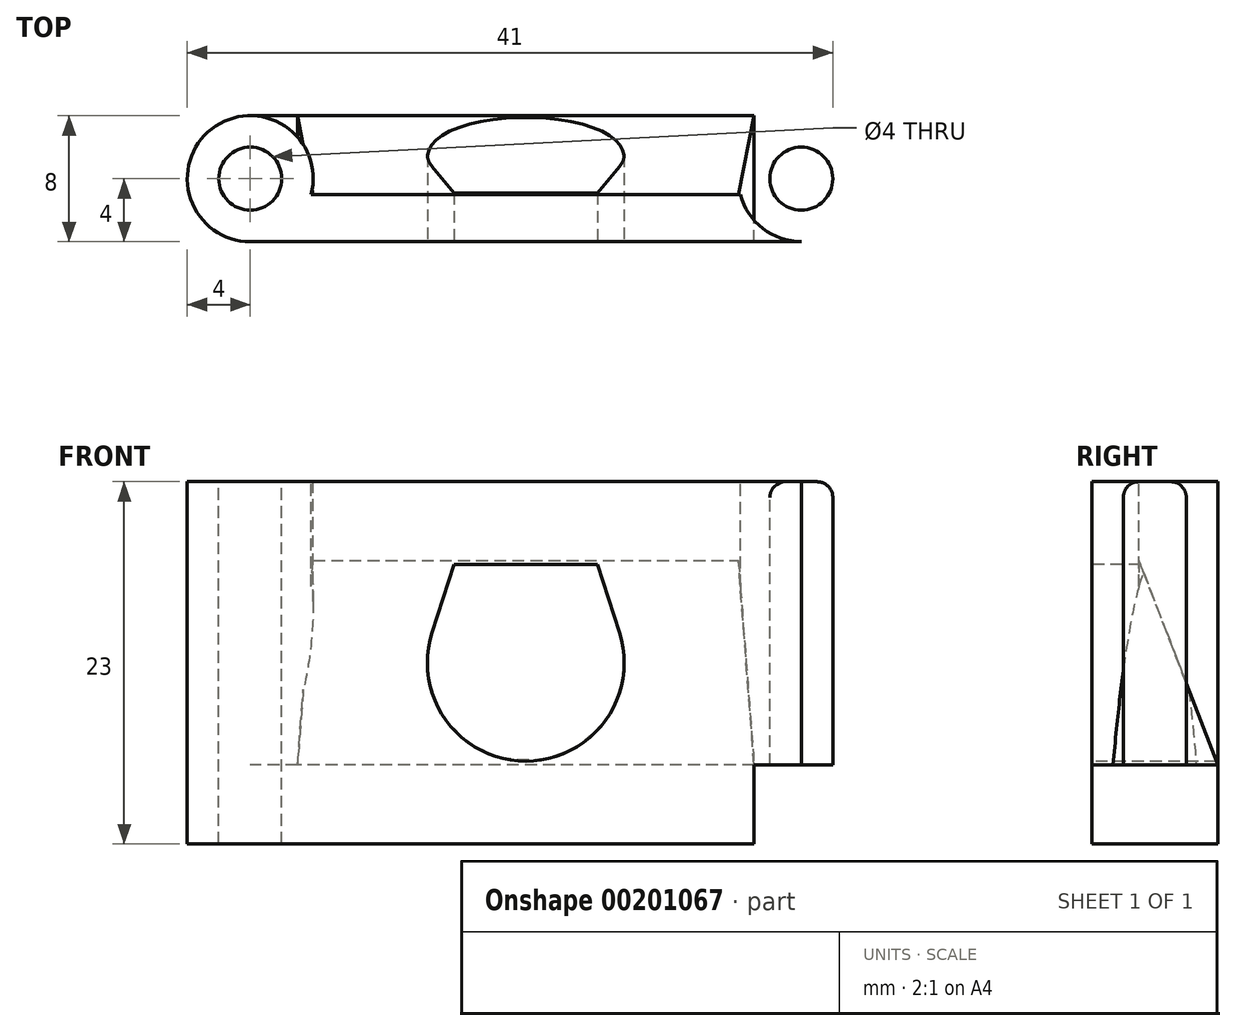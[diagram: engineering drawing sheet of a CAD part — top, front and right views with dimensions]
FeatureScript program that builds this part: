
annotation { "Feature Type Name" : "Feature", "Feature Type Description" : "" }
export const myFeature = defineFeature(function(context is Context, id is Id, definition is map)
    precondition{}
    {
        {
            var Q0;
            Q0=qCreatedBy(makeId("Top.planeOp"),FACE);
            var sketch = newSketch(context, id + "F0", { "sketchPlane" : qUnion([Q0])});
            skLineSegment(sketch, "E0.bottom", {"start": v(17.5, -4) * mm, "end": v(-17.5, -4) * mm});
            skLineSegment(sketch, "E0.top", {"start": v(17.5, 4) * mm, "end": v(-17.5, 4) * mm});
            skPoint(sketch, "E0.middle", {"position": v(0, 0) * mm});
            skArc(sketch, "E1", {"start": v(-17.5, 4) * mm, "mid": v(-21.5, 0) * mm, "end": v(-17.5, -4) * mm});
            skCircle(sketch, "E2", {"center": v(-17.5, 0) * mm, "radius": 2 * mm});
            skArc(sketch, "E3.MirrorCS", {"start": v(17.5, 4) * mm, "mid": v(21.5, 0) * mm, "end": v(17.5, -4) * mm});
            skCircle(sketch, "E4.MirrorC", {"center": v(17.5, 0) * mm, "radius": 2 * mm});
            skPoint(sketch, "E5.start.orphan", {"position": v(-15.5, 0) * mm});
            skPoint(sketch, "E6.start.orphan", {"position": v(15.5, 0) * mm});
            skPoint(sketch, "E7.start.orphan", {"position": v(-15.5, -4) * mm});
            skPoint(sketch, "E8.orphan", {"position": v(15.5, -4) * mm});
            skPoint(sketch, "E9.start.orphan", {"position": v(15.5, 4) * mm});
            skLineSegment(sketch, "E10", {"start": v(14.5, -4) * mm, "end": v(14.5, 4) * mm});
            skLineSegment(sketch, "E11", {"start": v(-14.5, 4) * mm, "end": v(-14.5, -4) * mm});
            skSolve(sketch);
        }
        {
            var Q0;
            Q0=qCreatedBy(makeId("Top.planeOp"),FACE);
            cPlane(context, id + "F1", {"entities" : qUnion([Q0]), "cplaneType" : CPlaneType.OFFSET, "offset" : 13 * mm, "width" : 150 * mm, "height" : 150 * mm});
        }
        {
            var Q0;
            Q0=qCreatedBy(id+"F1.planeOp",FACE);
            var sketch = newSketch(context, id + "F2", { "sketchPlane" : qUnion([Q0])});
            skLineSegment(sketch, "E12.bottom", {"start": v(-17.5, -4) * mm, "end": v(17.5, -4) * mm});
            skLineSegment(sketch, "E12.top", {"start": v(-13.63, -1) * mm, "end": v(13.63, -1) * mm});
            skCircle(sketch, "E13", {"center": v(-17.5, 0) * mm, "radius": 4 * mm});
            skCircle(sketch, "E14", {"center": v(-17.5, 0) * mm, "radius": 2 * mm});
            skCircle(sketch, "E15.MirrorC", {"center": v(17.5, 0) * mm, "radius": 4 * mm});
            skCircle(sketch, "E16.MirrorC", {"center": v(17.5, 0) * mm, "radius": 2 * mm});
            skLineSegment(sketch, "E17", {"start": v(-13.5, -1) * mm, "end": v(-13.5, -4) * mm});
            skLineSegment(sketch, "E18", {"start": v(13.5, -1) * mm, "end": v(13.5, -4) * mm});
            skPoint(sketch, "E19.orphan", {"position": v(-13.5, 0) * mm});
            skPoint(sketch, "E20.orphan", {"position": v(13.5, 0) * mm});
            skSolve(sketch);
        }
        {
            var Q0;
            {var subQ0=sQuery(id+"F0.wireOp",EDGE,"E10");Q0=makeQuery(id+"F0.imprint","IMPRINT",FACE,{"disambiguationData":[TD([[makeQuery(id+"F0.imprint","IMPRINT",EDGE,{"derivedFrom":subQ0}),1.0]])]});}
            var Q1;
            {var subQ0=sQuery(id+"F2.wireOp",EDGE,"E17");Q1=makeQuery(id+"F2.imprint","IMPRINT",FACE,{"disambiguationData":[TD([[makeQuery(id+"F2.imprint","IMPRINT",EDGE,{"derivedFrom":subQ0}),1.0]])]});}
            loft(context, id + "F3", {"sheetProfilesArray" : [{ "sheetProfileEntities" : qUnion([Q0]) }, { "sheetProfileEntities" : qUnion([Q1]) }]});
        }
        {
            var Q0;
            {var subQ3=sQuery(id+"F2.wireOp",EDGE,"E18");Q0=makeQuery(id+"F2.imprint","IMPRINT",FACE,{"disambiguationData":[TD([[makeQuery(id+"F2.imprint","IMPRINT",EDGE,{"derivedFrom":subQ3}),1.0]])]});}
            var Q1;
            Q1=makeQuery(id+"F2.imprint","IMPRINT",FACE,{"disambiguationData":[TD([[makeQuery(id+"F2.imprint","IMPRINT",EDGE,{"derivedFrom":sQuery(id+"F2.wireOp",EDGE,"E16.MirrorC")}),1.0]])]});
            var Q2;
            Q2=makeQuery(id+"F2.imprint","IMPRINT",FACE,{"disambiguationData":[TD([[makeQuery(id+"F2.imprint","IMPRINT",EDGE,{"derivedFrom":sQuery(id+"F2.wireOp",EDGE,"E14")}),-1.0]])]});
            var Q3;
            {var subQ3=sQuery(id+"F2.wireOp",EDGE,"E17");Q3=makeQuery(id+"F2.imprint","IMPRINT",FACE,{"disambiguationData":[TD([[makeQuery(id+"F2.imprint","IMPRINT",EDGE,{"derivedFrom":subQ3}),-1.0]])]});}
            extrude(context, id + "F4", {"entities" : qUnion([Q0, Q1, Q2, Q3]), "operationType" : NewBodyOperationType.ADD, "oppositeDirection" : true, "depth" : 13 * mm});
        }
        {
            var Q0;
            {var subQ0=sQuery(id+"F2.wireOp",EDGE,"E12.bottom");var subQ1=sQuery(id+"F2.wireOp",EDGE,"E18");var subQ2=sQuery(id+"F2.wireOp",EDGE,"E17");Q0=makeQuery(id+"F4.boolean.opBoolean","MERGE",FACE,{"derivedFrom":[makeQuery(id+"F3.opLoft","SWEPT_FACE",FACE,{"disambiguationData":[OSD([sQuery(id+"F0.wireOp",EDGE,"E0.bottom"),sQuery(id+"F0.wireOp",EDGE,"E10"),sQuery(id+"F0.wireOp",EDGE,"E11"),subQ0,subQ2,subQ1])]}),makeQuery(id+"F4.opExtrude","SWEPT_FACE",FACE,{"disambiguationData":[OSD([subQ0]),TDD([makeQuery(id+"F2.imprint","IMPRINT",EDGE,{"disambiguationData":[TD([[makeQuery(id+"F2.imprint","INTERSECT",VERTEX,{"derivedFrom":[subQ0,sQuery(id+"F2.wireOp",EDGE,"E13")]}),-1.0]])],"derivedFrom":subQ0})])]}),makeQuery(id+"F4.opExtrude","SWEPT_FACE",FACE,{"disambiguationData":[OSD([subQ0]),TDD([makeQuery(id+"F2.imprint","IMPRINT",EDGE,{"disambiguationData":[TD([[makeQuery(id+"F2.imprint","INTERSECT",VERTEX,{"derivedFrom":[subQ0,sQuery(id+"F2.wireOp",EDGE,"E15.MirrorC")]}),1.0]])],"derivedFrom":subQ0})])]})]});}
            var sketch = newSketch(context, id + "F5", { "sketchPlane" : qUnion([Q0])});
            skArc(sketch, "E21", {"start": v(-5.94, 8.43) * mm, "mid": v(0, 0.25) * mm, "end": v(5.94, 8.43) * mm});
            skLineSegment(sketch, "E22", {"start": v(0, 13) * mm, "end": v(0, 0) * mm, "construction": true});
            skArc(sketch, "E23.cCircle", {"start": v(-5.94, 8.43) * mm, "mid": v(0, 0.25) * mm, "end": v(5.94, 8.43) * mm, "construction": true});
            skLineSegment(sketch, "E23.0", {"start": v(-4.54, 12.75) * mm, "end": v(4.54, 12.75) * mm});
            skLineSegment(sketch, "E23.1", {"start": v(4.54, 12.75) * mm, "end": v(5.94, 8.43) * mm});
            skLineSegment(sketch, "E23.4", {"start": v(-5.94, 8.43) * mm, "end": v(-4.54, 12.75) * mm});
            skPoint(sketch, "E23.0.midPoint", {"position": v(0, 12.75) * mm});
            skPoint(sketch, "E24.orphan", {"position": v(7.35, 4.11) * mm});
            skPoint(sketch, "E25.orphan", {"position": v(-7.35, 4.11) * mm});
            skSolve(sketch);
        }
        {
            var Q0;
            Q0=makeQuery(id+"F5.imprint","IMPRINT",FACE,{"disambiguationData":[TD([[makeQuery(id+"F5.imprint","IMPRINT",EDGE,{"derivedFrom":sQuery(id+"F5.wireOp",EDGE,"E21")}),1.0]])]});
            extrude(context, id + "F6", {"entities" : qUnion([Q0]), "operationType" : NewBodyOperationType.REMOVE, "oppositeDirection" : true, "depth" : 25 * mm});
        }
        {
            var Q0;
            {var subQ0=sQuery(id+"F2.wireOp",EDGE,"E17");Q0=makeQuery(id+"F2.imprint","IMPRINT",FACE,{"disambiguationData":[TD([[makeQuery(id+"F2.imprint","IMPRINT",EDGE,{"derivedFrom":subQ0}),1.0]])]});}
            var Q1;
            {var subQ3=sQuery(id+"F2.wireOp",EDGE,"E17");Q1=makeQuery(id+"F2.imprint","IMPRINT",FACE,{"disambiguationData":[TD([[makeQuery(id+"F2.imprint","IMPRINT",EDGE,{"derivedFrom":subQ3}),-1.0]])]});}
            var Q2;
            Q2=makeQuery(id+"F2.imprint","IMPRINT",FACE,{"disambiguationData":[TD([[makeQuery(id+"F2.imprint","IMPRINT",EDGE,{"derivedFrom":sQuery(id+"F2.wireOp",EDGE,"E14")}),-1.0]])]});
            var Q3;
            Q3=makeQuery(id+"F2.imprint","IMPRINT",FACE,{"disambiguationData":[TD([[makeQuery(id+"F2.imprint","IMPRINT",EDGE,{"derivedFrom":sQuery(id+"F2.wireOp",EDGE,"E16.MirrorC")}),1.0]])]});
            var Q4;
            {var subQ3=sQuery(id+"F2.wireOp",EDGE,"E18");Q4=makeQuery(id+"F2.imprint","IMPRINT",FACE,{"disambiguationData":[TD([[makeQuery(id+"F2.imprint","IMPRINT",EDGE,{"derivedFrom":subQ3}),1.0]])]});}
            extrude(context, id + "F7", {"entities" : qUnion([Q0, Q1, Q2, Q3, Q4]), "operationType" : NewBodyOperationType.ADD, "depth" : 5 * mm});
        }
        {
            var Q0;
            {var subQ0=sQuery(id+"F0.wireOp",EDGE,"E10");Q0=makeQuery(id+"F0.imprint","IMPRINT",FACE,{"disambiguationData":[TD([[makeQuery(id+"F0.imprint","IMPRINT",EDGE,{"derivedFrom":subQ0}),1.0]])]});}
            var Q1;
            {var subQ0=sQuery(id+"F0.wireOp",EDGE,"E1");Q1=makeQuery(id+"F0.imprint","IMPRINT",FACE,{"disambiguationData":[TD([[makeQuery(id+"F0.imprint","IMPRINT",EDGE,{"derivedFrom":subQ0}),1.0]])]});}
            var Q2;
            {var subQ0=sQuery(id+"F0.wireOp",EDGE,"E3.MirrorCS");Q2=makeQuery(id+"F0.imprint","IMPRINT",FACE,{"disambiguationData":[TD([[makeQuery(id+"F0.imprint","IMPRINT",EDGE,{"derivedFrom":subQ0}),-1.0]])]});}
            extrude(context, id + "F8", {"entities" : qUnion([Q0, Q1, Q2]), "operationType" : NewBodyOperationType.ADD, "oppositeDirection" : true, "depth" : 5 * mm});
        }
        {
            var Q0;
            Q0=makeQuery(id+"F7.opExtrude","CAP_EDGE",EDGE,{"disambiguationData":[OSD([sQuery(id+"F2.wireOp",EDGE,"E12.top")])],"isStart":false});
            var Q1;
            Q1=makeQuery(id+"F7.opExtrude","CAP_EDGE",EDGE,{"disambiguationData":[OSD([sQuery(id+"F2.wireOp",EDGE,"E15.MirrorC")])],"isStart":false});
            var Q2;
            Q2=makeQuery(id+"F8.opExtrude","CAP_EDGE",EDGE,{"disambiguationData":[OSD([sQuery(id+"F0.wireOp",EDGE,"E0.top")])],"isStart":false});
            var Q3;
            Q3=makeQuery(id+"F7.opExtrude","CAP_EDGE",EDGE,{"disambiguationData":[OSD([sQuery(id+"F2.wireOp",EDGE,"E14")])],"isStart":false});
            var Q4;
            Q4=makeQuery(id+"F7.opExtrude","CAP_EDGE",EDGE,{"disambiguationData":[OSD([sQuery(id+"F2.wireOp",EDGE,"E16.MirrorC")])],"isStart":false});
            var Q5;
            Q5=makeQuery(id+"F6.boolean.opBoolean","COPY",EDGE,{"derivedFrom":makeQuery(id+"F6.opExtrude","CAP_EDGE",EDGE,{"disambiguationData":[OSD([sQuery(id+"F5.wireOp",EDGE,"E21")])],"isStart":true})});
            var Q6;
            Q6=makeQuery(id+"F6.boolean.opBoolean","INTERSECT",EDGE,{"derivedFrom":[makeQuery(id+"F3.opLoft","SWEPT_FACE",FACE,{"disambiguationData":[OSD([sQuery(id+"F0.wireOp",EDGE,"E0.top"),sQuery(id+"F0.wireOp",EDGE,"E10"),sQuery(id+"F0.wireOp",EDGE,"E11"),sQuery(id+"F2.wireOp",EDGE,"E12.top"),sQuery(id+"F2.wireOp",EDGE,"E17"),sQuery(id+"F2.wireOp",EDGE,"E18")])]}),makeQuery(id+"F6.opExtrude","SWEPT_FACE",FACE,{"disambiguationData":[OSD([sQuery(id+"F5.wireOp",EDGE,"E21")])]})]});
            var Q7;
            {var subQ0=sQuery(id+"F0.wireOp",EDGE,"E0.top");Q7=makeQuery(id+"F8.boolean.opBoolean","MERGE",EDGE,{"derivedFrom":[makeQuery(id+"F3.opLoft","MID_CAP_EDGE",EDGE,{"disambiguationData":[OSD([subQ0,sQuery(id+"F0.wireOp",EDGE,"E10"),sQuery(id+"F0.wireOp",EDGE,"E11")])],"capPos":0.0}),makeQuery(id+"F8.opExtrude","CAP_EDGE",EDGE,{"disambiguationData":[OSD([subQ0])],"isStart":true})]});}
            var Q8;
            Q8=makeQuery(id+"F6.boolean.opBoolean","COPY",EDGE,{"derivedFrom":makeQuery(id+"F6.opExtrude","CAP_EDGE",EDGE,{"disambiguationData":[OSD([sQuery(id+"F5.wireOp",EDGE,"E23.0")])],"isStart":true})});
            var Q9;
            Q9=makeQuery(id+"F6.boolean.opBoolean","INTERSECT",EDGE,{"derivedFrom":[makeQuery(id+"F3.opLoft","SWEPT_FACE",FACE,{"disambiguationData":[OSD([sQuery(id+"F0.wireOp",EDGE,"E0.top"),sQuery(id+"F0.wireOp",EDGE,"E10"),sQuery(id+"F0.wireOp",EDGE,"E11"),sQuery(id+"F2.wireOp",EDGE,"E12.top"),sQuery(id+"F2.wireOp",EDGE,"E17"),sQuery(id+"F2.wireOp",EDGE,"E18")])]}),makeQuery(id+"F6.opExtrude","SWEPT_FACE",FACE,{"disambiguationData":[OSD([sQuery(id+"F5.wireOp",EDGE,"E23.0")])]})]});
            fillet(context, id + "F9", {"entities" : qUnion([Q0, Q1, Q2, Q3, Q4, Q5, Q6, Q7, Q8, Q9]), "radius" : 1 * mm, "tangentPropagation" : true, "allowEdgeOverflow" : false});
        }
    });
